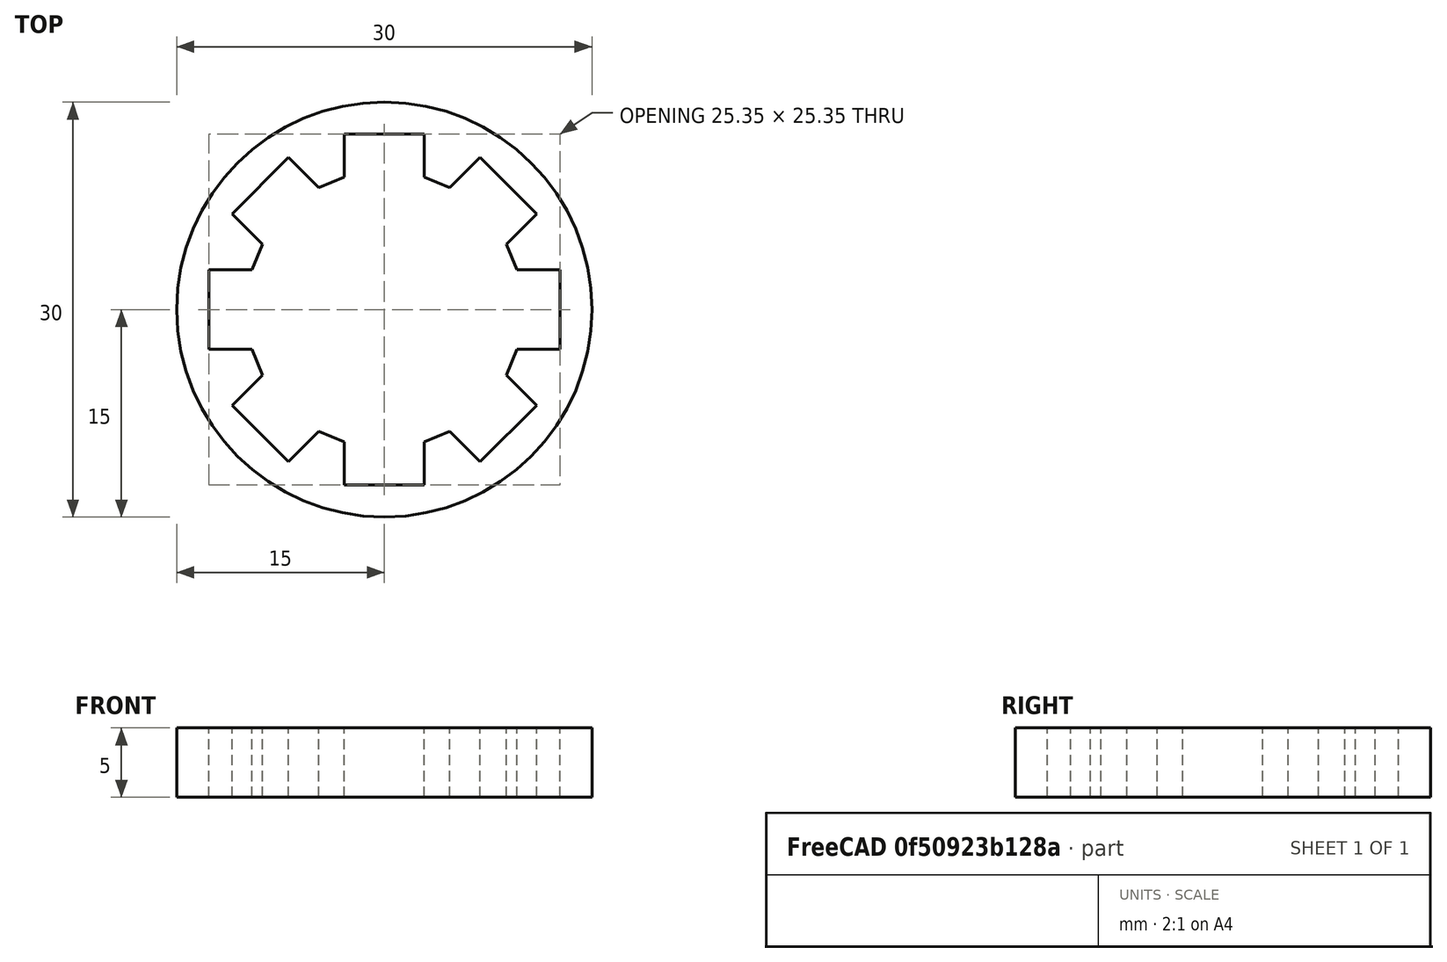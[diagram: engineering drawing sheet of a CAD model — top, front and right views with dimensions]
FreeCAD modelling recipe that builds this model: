
FCSTD DOCUMENT  (FreeCAD 0.17RUnknown)
Label: gear1
License: All rights reserved
LicenseURL: http://en.wikipedia.org/wiki/All_rights_reserved
objects: Sketcher::SketchObject×1, PartDesign::Pad×1, PartDesign::Body×1
note: 4 computed .brp shape members not serialized (recipe doc carries the construction recipe); baked Part::Feature solids carry a one-line shape summary decoded from their .brp

FEATURE [Sketcher::SketchObject] Sketch
  MapMode = 5
  Support = -> [XY_Plane]
  sketch-geometry (39):
    g0: Circle CenterX=0 CenterY=0 CenterZ=0 NormalX=0 NormalY=0 NormalZ=1 AngleXU=0 Radius=15
    g1: LineSegment StartX=0 StartY=12.6761 StartZ=0 EndX=2.88377 EndY=12.6761 EndZ=0
    g2: LineSegment StartX=2.88377 StartY=12.6761 StartZ=0 EndX=2.88377 EndY=9.57517 EndZ=0
    g3: LineSegment StartX=2.88377 StartY=9.57517 StartZ=0 EndX=4.73153 EndY=8.8098 EndZ=0
    g4: LineSegment StartX=4.73153 StartY=8.8098 StartZ=0 EndX=6.92423 EndY=11.0025 EndZ=0
    g5: LineSegment StartX=6.92423 StartY=11.0025 StartZ=0 EndX=11.0025 EndY=6.92423 EndZ=0
    g6: LineSegment StartX=11.0025 StartY=6.92423 StartZ=0 EndX=8.8098 EndY=4.73153 EndZ=0
    g7: LineSegment StartX=8.8098 StartY=4.73153 StartZ=0 EndX=9.57517 EndY=2.88377 EndZ=0
    g8: LineSegment StartX=9.57517 StartY=2.88377 StartZ=0 EndX=12.6761 EndY=2.88377 EndZ=0
    g9: LineSegment StartX=12.6761 StartY=2.88377 StartZ=0 EndX=12.6761 EndY=0 EndZ=0
    g10: ArcOfCircle [constr] CenterX=0 CenterY=0 CenterZ=0 NormalX=0 NormalY=0 NormalZ=1 AngleXU=0 Radius=10 StartAngle=0 EndAngle=1.5708
    g11: ArcOfCircle [constr] CenterX=0 CenterY=0 CenterZ=0 NormalX=0 NormalY=0 NormalZ=1 AngleXU=0 Radius=13 StartAngle=0 EndAngle=1.5708
    g12: LineSegment StartX=12.6761 StartY=0 StartZ=0 EndX=12.6761 EndY=-2.88377 EndZ=0
    g13: LineSegment StartX=12.6761 StartY=-2.88377 StartZ=0 EndX=9.57517 EndY=-2.88377 EndZ=0
    g14: LineSegment StartX=9.57517 StartY=-2.88377 StartZ=0 EndX=8.8098 EndY=-4.73153 EndZ=0
    g15: LineSegment StartX=8.8098 StartY=-4.73153 StartZ=0 EndX=11.0025 EndY=-6.92423 EndZ=0
    g16: LineSegment StartX=11.0025 StartY=-6.92423 StartZ=0 EndX=6.92423 EndY=-11.0025 EndZ=0
    g17: LineSegment StartX=6.92423 StartY=-11.0025 StartZ=0 EndX=4.73153 EndY=-8.8098 EndZ=0
    g18: LineSegment StartX=4.73153 StartY=-8.8098 StartZ=0 EndX=2.88377 EndY=-9.57517 EndZ=0
    g19: LineSegment StartX=2.88377 StartY=-9.57517 StartZ=0 EndX=2.88377 EndY=-12.6761 EndZ=0
    g20: LineSegment StartX=2.88377 StartY=-12.6761 StartZ=0 EndX=0 EndY=-12.6761 EndZ=0
    g21: LineSegment StartX=0 StartY=12.6761 StartZ=0 EndX=-2.88377 EndY=12.6761 EndZ=0
    g22: LineSegment StartX=-2.88377 StartY=12.6761 StartZ=0 EndX=-2.88377 EndY=9.57517 EndZ=0
    g23: LineSegment StartX=-2.88377 StartY=9.57517 StartZ=0 EndX=-4.73153 EndY=8.8098 EndZ=0
    g24: LineSegment StartX=-4.73153 StartY=8.8098 StartZ=0 EndX=-6.92423 EndY=11.0025 EndZ=0
    g25: LineSegment StartX=-6.92423 StartY=11.0025 StartZ=0 EndX=-11.0025 EndY=6.92423 EndZ=0
    g26: LineSegment StartX=-11.0025 StartY=6.92423 StartZ=0 EndX=-8.8098 EndY=4.73153 EndZ=0
    g27: LineSegment StartX=-8.8098 StartY=4.73153 StartZ=0 EndX=-9.57517 EndY=2.88377 EndZ=0
    g28: LineSegment StartX=-9.57517 StartY=2.88377 StartZ=0 EndX=-12.6761 EndY=2.88377 EndZ=0
    g29: LineSegment StartX=-12.6761 StartY=2.88377 StartZ=0 EndX=-12.6761 EndY=0 EndZ=0
    g30: LineSegment StartX=-12.6761 StartY=0 StartZ=0 EndX=-12.6761 EndY=-2.88377 EndZ=0
    g31: LineSegment StartX=-12.6761 StartY=-2.88377 StartZ=0 EndX=-9.57517 EndY=-2.88377 EndZ=0
    g32: LineSegment StartX=-9.57517 StartY=-2.88377 StartZ=0 EndX=-8.8098 EndY=-4.73153 EndZ=0
    g33: LineSegment StartX=-8.8098 StartY=-4.73153 StartZ=0 EndX=-11.0025 EndY=-6.92423 EndZ=0
    g34: LineSegment StartX=-11.0025 StartY=-6.92423 StartZ=0 EndX=-6.92423 EndY=-11.0025 EndZ=0
    g35: LineSegment StartX=-6.92423 StartY=-11.0025 StartZ=0 EndX=-4.73153 EndY=-8.8098 EndZ=0
    g36: LineSegment StartX=-4.73153 StartY=-8.8098 StartZ=0 EndX=-2.88377 EndY=-9.57517 EndZ=0
    g37: LineSegment StartX=-2.88377 StartY=-9.57517 StartZ=0 EndX=-2.88377 EndY=-12.6761 EndZ=0
    g38: LineSegment StartX=-2.88377 StartY=-12.6761 StartZ=0 EndX=0 EndY=-12.6761 EndZ=0
  constraints (96):
    c: Coincident(g0,g-1)
    c: Radius(g0) = 15
    c: Coincident(g1,g2)
    c: Coincident(g2,g3)
    c: Coincident(g3,g4)
    c: Coincident(g4,g5)
    c: Coincident(g5,g6)
    c: Coincident(g6,g7)
    c: Coincident(g8,g9)
    c: Perpendicular(g2,g1)
    c: Perpendicular(g5,g4)
    c: Perpendicular(g5,g6)
    c: Perpendicular(g-2,g1)
    c: Perpendicular(g-1,g9)
    c: PointOnObject(g1,g-2)
    c: PointOnObject(g9,g-1)
    c: Perpendicular(g9,g8)
    c: Distance(g3) = 2
    c: Distance(g7) = 2
    c: Coincident(g10,g-1)
    c: PointOnObject(g10,g-1)
    c: PointOnObject(g10,g-2)
    c: Radius(g10) = 10
    c: PointOnObject(g8,g10)
    c: PointOnObject(g7,g10)
    c: PointOnObject(g6,g10)
    c: PointOnObject(g3,g10)
    c: PointOnObject(g2,g10)
    c: Coincident(g11,g-1)
    c: PointOnObject(g11,g-1)
    c: PointOnObject(g11,g-2)
    c: Radius(g11) = 13
    c: PointOnObject(g8,g11)
    c: PointOnObject(g5,g11)
    c: PointOnObject(g4,g11)
    c: PointOnObject(g1,g11)
    c: Coincident(g9,g12)
    c: Coincident(g12,g13)
    c: Horizontal(g13)
    c: Coincident(g14,g15)
    c: Coincident(g15,g16)
    c: Coincident(g16,g17)
    c: Coincident(g17,g18)
    c: Coincident(g18,g19)
    c: Coincident(g19,g20)
    c: Symmetric(g8,g12,g-1)
    c: Symmetric(g8,g13,g-1)
    c: Symmetric(g7,g14,g-1)
    c: Symmetric(g14,g6,g-1)
    c: Symmetric(g15,g5,g-1)
    c: Symmetric(g16,g4,g-1)
    c: Symmetric(g3,g17,g-1)
    c: Symmetric(g18,g2,g-1)
    c: Symmetric(g19,g1,g-1)
    c: PointOnObject(g20,g-2)
    c: Perpendicular(g-2,g20)
    c: Coincident(g1,g21)
    c: Coincident(g21,g22)
    c: Coincident(g22,g23)
    c: Coincident(g23,g24)
    c: Coincident(g24,g25)
    c: Coincident(g25,g26)
    c: Coincident(g26,g27)
    c: Coincident(g28,g29)
    c: PointOnObject(g29,g-1)
    c: Symmetric(g1,g21,g-2)
    c: Symmetric(g2,g22,g-2)
    c: Symmetric(g23,g3,g-2)
    c: Symmetric(g24,g4,g-2)
    c: Symmetric(g25,g5,g-2)
    c: Symmetric(g6,g26,g-2)
    c: Symmetric(g27,g7,g-2)
    c: Symmetric(g28,g8,g-2)
    c: Symmetric(g28,g8,g-2)
    c: Perpendicular(g29,g-1)
    c: Coincident(g29,g30)
    c: Coincident(g30,g31)
    c: Coincident(g32,g33)
    c: Coincident(g33,g34)
    c: Coincident(g34,g35)
    c: Coincident(g35,g36)
    c: Coincident(g36,g37)
    c: Coincident(g37,g38)
    c: Coincident(g38,g20)
    c: Symmetric(g30,g8,g-1)
    c: Symmetric(g31,g8,g-1)
    c: Symmetric(g32,g7,g-1)
    c: Symmetric(g32,g6,g-1)
    c: Symmetric(g33,g5,g-1)
    c: Symmetric(g34,g4,g-1)
    c: Symmetric(g35,g3,g-1)
    c: Symmetric(g36,g2,g-1)
    c: Symmetric(g37,g1,g-1)
    c: Coincident(g7,g8)
    c: Angle(g3,g2) = 1.9635
    c: Angle(g7,g6) = 1.9635
FEATURE [PartDesign::Pad] Pad
  Length = 5
  Length2 = 100
  Profile = -> Sketch
  Type = 0
FEATURE [PartDesign::Body] Body
  Group = -> [Sketch,Pad]
  Origin = -> Origin
  Tip = -> Pad
